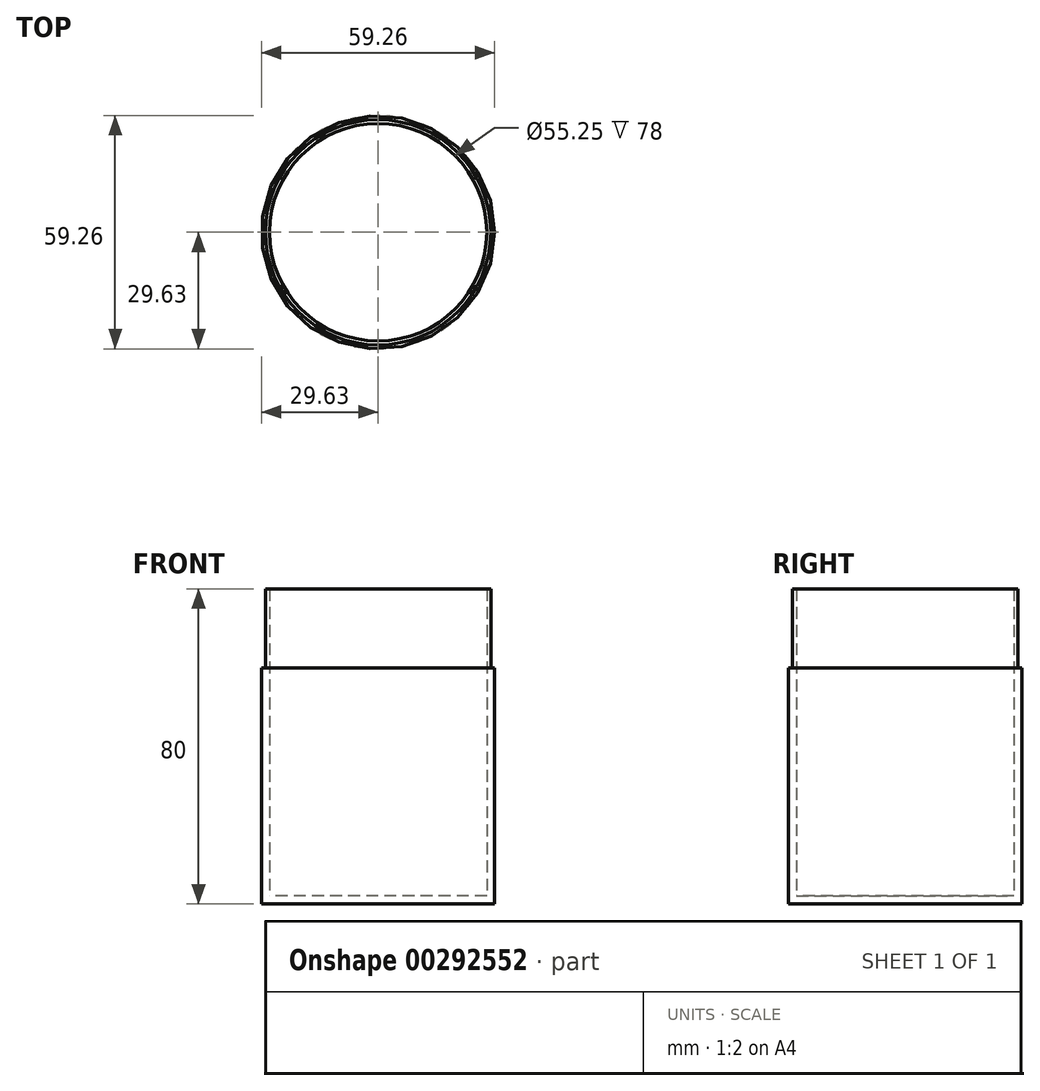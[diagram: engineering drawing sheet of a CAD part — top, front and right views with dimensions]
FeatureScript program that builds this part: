
annotation { "Feature Type Name" : "Feature", "Feature Type Description" : "" }
export const myFeature = defineFeature(function(context is Context, id is Id, definition is map)
    precondition{}
    {
        {
            var Q0;
            Q0=qCreatedBy(makeId("Top.planeOp"),FACE);
            var sketch = newSketch(context, id + "F0", { "sketchPlane" : qUnion([Q0])});
            skCircle(sketch, "E0", {"center": v(0, 0) * mm, "radius": 27.62 * mm});
            skCircle(sketch, "E1.0", {"center": v(0, 0) * mm, "radius": 29.62 * mm});
            skSolve(sketch);
        }
        {
            var Q0;
            Q0=makeQuery(id+"F0.imprint","IMPRINT",FACE,{"disambiguationData":[TD([[makeQuery(id+"F0.imprint","IMPRINT",EDGE,{"derivedFrom":sQuery(id+"F0.wireOp",EDGE,"E0")}),-1.0]])]});
            extrude(context, id + "F1", {"entities" : qUnion([Q0]), "depth" : 78 * mm});
        }
        {
            var Q0;
            Q0=qCreatedBy(makeId("Top.planeOp"),FACE);
            var sketch = newSketch(context, id + "F2", { "sketchPlane" : qUnion([Q0])});
            skCircle(sketch, "E2", {"center": v(0, 0) * mm, "radius": 29.63 * mm});
            skSolve(sketch);
        }
        {
            var Q0;
            Q0=qSketchRegion(id+"F2",true);
            extrude(context, id + "F3", {"entities" : qUnion([Q0]), "operationType" : NewBodyOperationType.ADD, "oppositeDirection" : true, "depth" : 2 * mm});
        }
        {
            var Q0;
            Q0=qCreatedBy(makeId("Top.planeOp"),FACE);
            cPlane(context, id + "F4", {"entities" : qUnion([Q0]), "cplaneType" : CPlaneType.OFFSET, "offset" : 78 * mm, "width" : 152.4 * mm, "height" : 152.4 * mm});
        }
        {
            var Q0;
            Q0=qCreatedBy(id+"F4.planeOp",FACE);
            var sketch = newSketch(context, id + "F5", { "sketchPlane" : qUnion([Q0])});
            skCircle(sketch, "E3.0", {"center": v(0, 0) * mm, "radius": 29.63 * mm});
            skCircle(sketch, "E4.0", {"center": v(0, 0) * mm, "radius": 28.63 * mm});
            skCircle(sketch, "E5.0", {"center": v(0, 0) * mm, "radius": 27.63 * mm});
            skSolve(sketch);
        }
        {
            var Q0;
            Q0=makeQuery(id+"F5.imprint","IMPRINT",FACE,{"disambiguationData":[TD([[makeQuery(id+"F5.imprint","IMPRINT",EDGE,{"derivedFrom":sQuery(id+"F5.wireOp",EDGE,"E3.0")}),1.0]])]});
            extrude(context, id + "F6", {"entities" : qUnion([Q0]), "operationType" : NewBodyOperationType.REMOVE, "oppositeDirection" : true, "depth" : 20 * mm});
        }
    });
